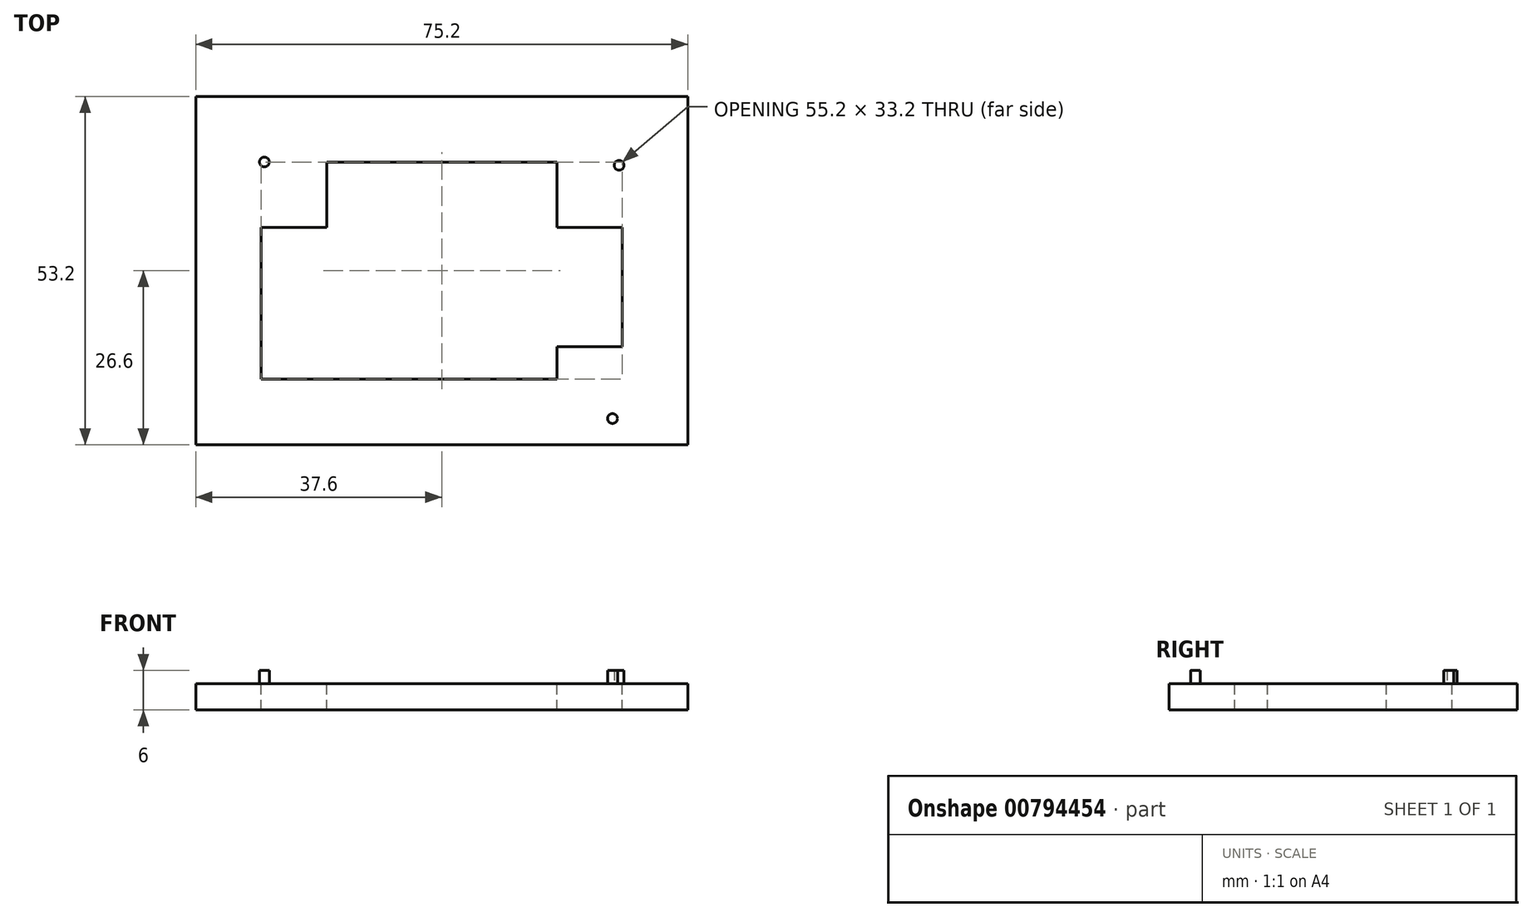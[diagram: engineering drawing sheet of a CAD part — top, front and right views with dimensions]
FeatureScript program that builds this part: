
annotation { "Feature Type Name" : "Feature", "Feature Type Description" : "" }
export const myFeature = defineFeature(function(context is Context, id is Id, definition is map)
    precondition{}
    {
        {
            var Q0;
            Q0=qCreatedBy(makeId("Top.planeOp"),FACE);
            var sketch = newSketch(context, id + "F0", { "sketchPlane" : qUnion([Q0])});
            skLineSegment(sketch, "E0.bottom", {"start": v(0, 0) * mm, "end": v(75.2, 0) * mm});
            skLineSegment(sketch, "E0.top", {"start": v(0, -53.2) * mm, "end": v(75.2, -53.2) * mm});
            skLineSegment(sketch, "E0.left", {"start": v(0, 0) * mm, "end": v(0, -53.2) * mm});
            skLineSegment(sketch, "E0.right", {"start": v(75.2, 0) * mm, "end": v(75.2, -53.2) * mm});
            skSolve(sketch);
        }
        {
            var Q0;
            Q0 = qSketchRegion(id + "F0", true);
            extrude(context, id + "F1", {"entities" : qUnion([Q0]), "depth" : 4 * mm, "offsetDistance" : 25 * mm});
        }
        {
            var Q0;
            Q0=makeQuery(id+"F1.opExtrude","CAP_FACE",FACE,{"disambiguationData":[OSD([sQuery(id+"F0.wireOp",EDGE,"E0.bottom"),sQuery(id+"F0.wireOp",EDGE,"E0.top"),sQuery(id+"F0.wireOp",EDGE,"E0.left"),sQuery(id+"F0.wireOp",EDGE,"E0.right")])],"isStart":false});
            var sketch = newSketch(context, id + "F2", { "sketchPlane" : qUnion([Q0])});
            skCircle(sketch, "E1", {"center": v(10.5, -10) * mm, "radius": 0.75 * mm});
            skCircle(sketch, "E2", {"center": v(63.7, -49.2) * mm, "radius": 0.75 * mm});
            skCircle(sketch, "E3", {"center": v(64.7, -10.5) * mm, "radius": 0.75 * mm});
            skSolve(sketch);
        }
        {
            var Q0;
            Q0 = qSketchRegion(id + "F2", true);
            extrude(context, id + "F3", {"entities" : qUnion([Q0]), "operationType" : NewBodyOperationType.ADD, "depth" : 2 * mm, "offsetDistance" : 25 * mm});
        }
        {
            var Q0;
            Q0=makeQuery(id+"F1.opExtrude","CAP_FACE",FACE,{"disambiguationData":[OSD([sQuery(id+"F0.wireOp",EDGE,"E0.bottom"),sQuery(id+"F0.wireOp",EDGE,"E0.top"),sQuery(id+"F0.wireOp",EDGE,"E0.left"),sQuery(id+"F0.wireOp",EDGE,"E0.right")])],"isStart":false});
            var sketch = newSketch(context, id + "F4", { "sketchPlane" : qUnion([Q0])});
            skLineSegment(sketch, "E4.bottom", {"start": v(10, -20) * mm, "end": v(20, -20) * mm});
            skLineSegment(sketch, "E4.top", {"start": v(10, -43.2) * mm, "end": v(55.2, -43.2) * mm});
            skLineSegment(sketch, "E4.left", {"start": v(10, -20) * mm, "end": v(10, -43.2) * mm});
            skLineSegment(sketch, "E4.right", {"start": v(55.2, -38.2) * mm, "end": v(55.2, -43.2) * mm});
            skLineSegment(sketch, "E5.top", {"start": v(20, -10) * mm, "end": v(55.2, -10) * mm});
            skLineSegment(sketch, "E5.left", {"start": v(20, -20) * mm, "end": v(20, -10) * mm});
            skLineSegment(sketch, "E5.right", {"start": v(55.2, -20) * mm, "end": v(55.2, -10) * mm});
            skLineSegment(sketch, "E6.bottom", {"start": v(55.2, -38.2) * mm, "end": v(65.2, -38.2) * mm});
            skLineSegment(sketch, "E6.top", {"start": v(55.2, -20) * mm, "end": v(65.2, -20) * mm});
            skLineSegment(sketch, "E6.right", {"start": v(65.2, -38.2) * mm, "end": v(65.2, -20) * mm});
            skSolve(sketch);
        }
        {
            var Q0;
            Q0 = qSketchRegion(id + "F4", true);
            extrude(context, id + "F5", {"entities" : qUnion([Q0]), "operationType" : NewBodyOperationType.REMOVE, "oppositeDirection" : true, "depth" : 25 * mm, "offsetDistance" : 25 * mm});
        }
    });
